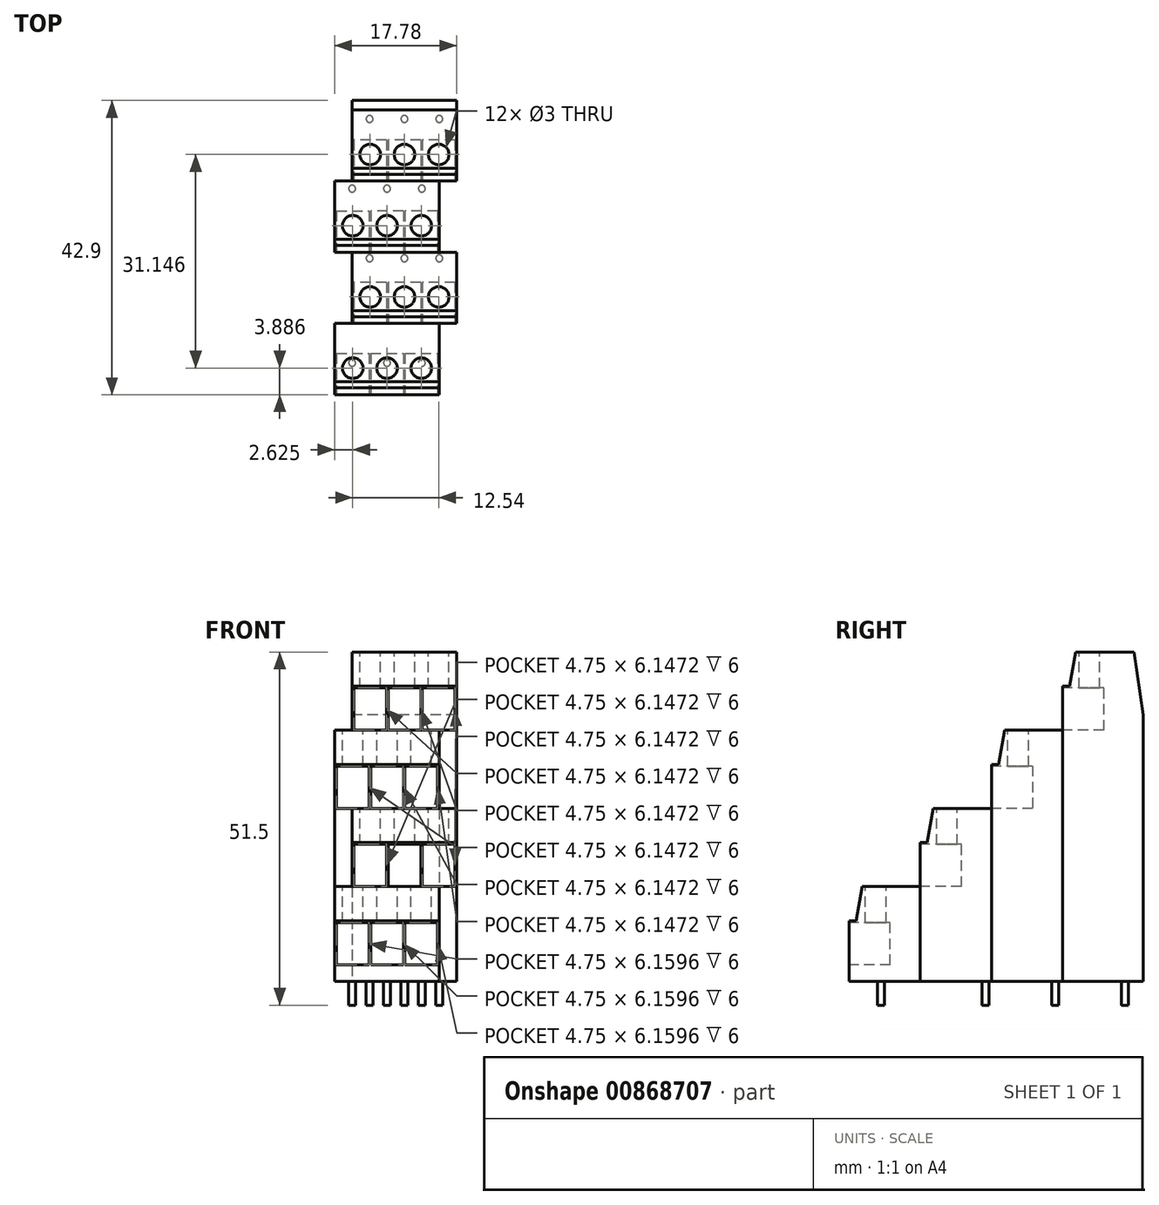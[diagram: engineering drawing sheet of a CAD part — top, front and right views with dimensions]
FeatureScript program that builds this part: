
annotation { "Feature Type Name" : "Feature", "Feature Type Description" : "" }
export const myFeature = defineFeature(function(context is Context, id is Id, definition is map)
    precondition{}
    {
        {
            var Q0;
            Q0=qCreatedBy(makeId("Right.planeOp"),FACE);
            var sketch = newSketch(context, id + "F0", { "sketchPlane" : qUnion([Q0])});
            skLineSegment(sketch, "E0.bottom", {"start": v(1.88, 24.08) * mm, "end": v(10.38, 24.08) * mm});
            skLineSegment(sketch, "E0.top", {"start": v(-31.15, -23.92) * mm, "end": v(11.75, -23.92) * mm});
            skLineSegment(sketch, "E0.left", {"start": v(-31.15, -15.12) * mm, "end": v(-31.15, -23.92) * mm});
            skLineSegment(sketch, "E0.right", {"start": v(11.75, 14.92) * mm, "end": v(11.75, -23.92) * mm});
            skPoint(sketch, "E0.middle", {"position": v(-0.86, 0) * mm});
            skLineSegment(sketch, "E1", {"start": v(-31.15, -15.12) * mm, "end": v(-30.15, -15.12) * mm});
            skLineSegment(sketch, "E2", {"start": v(-30.15, -15.12) * mm, "end": v(-29.26, -10.12) * mm});
            skLineSegment(sketch, "E3", {"start": v(-29.26, -10.12) * mm, "end": v(-20.76, -10.12) * mm});
            skLineSegment(sketch, "E4", {"start": v(-20.76, -10.12) * mm, "end": v(-20.76, -3.72) * mm});
            skLineSegment(sketch, "E5", {"start": v(-20.76, -3.72) * mm, "end": v(-19.76, -3.72) * mm});
            skLineSegment(sketch, "E6", {"start": v(-19.76, -3.72) * mm, "end": v(-18.88, 1.28) * mm});
            skLineSegment(sketch, "E7", {"start": v(-18.88, 1.28) * mm, "end": v(-10.38, 1.28) * mm});
            skLineSegment(sketch, "E8", {"start": v(-10.38, 1.28) * mm, "end": v(-10.38, 7.68) * mm});
            skLineSegment(sketch, "E9", {"start": v(-10.38, 7.68) * mm, "end": v(-9.38, 7.68) * mm});
            skLineSegment(sketch, "E10", {"start": v(-9.38, 7.68) * mm, "end": v(-8.5, 12.68) * mm});
            skLineSegment(sketch, "E11", {"start": v(-8.5, 12.68) * mm, "end": v(0, 12.68) * mm});
            skLineSegment(sketch, "E12", {"start": v(0, 12.68) * mm, "end": v(0, 19.08) * mm});
            skLineSegment(sketch, "E13", {"start": v(0, 19.08) * mm, "end": v(1, 19.08) * mm});
            skLineSegment(sketch, "E14", {"start": v(1, 19.08) * mm, "end": v(1.88, 24.08) * mm});
            skLineSegment(sketch, "E15", {"start": v(10.38, 24.08) * mm, "end": v(11.75, 14.92) * mm});
            skSolve(sketch);
        }
        {
            var Q0;
            Q0 = qSketchRegion(id + "F0", true);
            extrude(context, id + "F1", {"entities" : qUnion([Q0]), "endBound" : BoundingType.SYMMETRIC, "depth" : 17.78 * mm, "offsetDistance" : 25.4 * mm});
        }
        {
            var Q0;
            Q0=makeQuery(id+"F1.opExtrude","CAP_FACE",FACE,{"disambiguationData":[OSD([sQuery(id+"F0.wireOp",EDGE,"E0.bottom"),sQuery(id+"F0.wireOp",EDGE,"E0.top"),sQuery(id+"F0.wireOp",EDGE,"E0.left"),sQuery(id+"F0.wireOp",EDGE,"E0.right"),sQuery(id+"F0.wireOp",EDGE,"E1"),sQuery(id+"F0.wireOp",EDGE,"E2"),sQuery(id+"F0.wireOp",EDGE,"E3"),sQuery(id+"F0.wireOp",EDGE,"E4"),sQuery(id+"F0.wireOp",EDGE,"E5"),sQuery(id+"F0.wireOp",EDGE,"E6"),sQuery(id+"F0.wireOp",EDGE,"E7"),sQuery(id+"F0.wireOp",EDGE,"E8"),sQuery(id+"F0.wireOp",EDGE,"E9"),sQuery(id+"F0.wireOp",EDGE,"E10"),sQuery(id+"F0.wireOp",EDGE,"E11"),sQuery(id+"F0.wireOp",EDGE,"E12"),sQuery(id+"F0.wireOp",EDGE,"E13"),sQuery(id+"F0.wireOp",EDGE,"E14"),sQuery(id+"F0.wireOp",EDGE,"E15")])],"isStart":true});
            var sketch = newSketch(context, id + "F2", { "sketchPlane" : qUnion([Q0])});
            skLineSegment(sketch, "E16", {"start": v(20.76, -10.12) * mm, "end": v(20.76, -23.92) * mm});
            skLineSegment(sketch, "E17", {"start": v(0, 12.68) * mm, "end": v(0, -23.92) * mm});
            skLineSegment(sketch, "E18", {"start": v(10.38, 1.28) * mm, "end": v(10.38, -23.92) * mm});
            skSolve(sketch);
        }
        {
            var Q0;
            {var subQ1=sQuery(id+"F2.wireOp",EDGE,"E17");Q0=makeQuery(id+"F2.imprint","IMPRINT",FACE,{"disambiguationData":[TD([[makeQuery(id+"F2.imprint","IMPRINT",EDGE,{"derivedFrom":subQ1}),-1.0]])]});}
            var Q1;
            {var subQ1=sQuery(id+"F2.wireOp",EDGE,"E16");Q1=makeQuery(id+"F2.imprint","IMPRINT",FACE,{"disambiguationData":[TD([[makeQuery(id+"F2.imprint","IMPRINT",EDGE,{"derivedFrom":subQ1}),-1.0]])]});}
            extrude(context, id + "F3", {"entities" : qUnion([Q0, Q1]), "operationType" : NewBodyOperationType.REMOVE, "oppositeDirection" : true, "depth" : 2.54 * mm, "offsetDistance" : 25.4 * mm});
        }
        {
            var Q0;
            Q0=makeQuery(id+"F1.opExtrude","CAP_FACE",FACE,{"disambiguationData":[OSD([sQuery(id+"F0.wireOp",EDGE,"E0.bottom"),sQuery(id+"F0.wireOp",EDGE,"E0.top"),sQuery(id+"F0.wireOp",EDGE,"E0.left"),sQuery(id+"F0.wireOp",EDGE,"E0.right"),sQuery(id+"F0.wireOp",EDGE,"E1"),sQuery(id+"F0.wireOp",EDGE,"E2"),sQuery(id+"F0.wireOp",EDGE,"E3"),sQuery(id+"F0.wireOp",EDGE,"E4"),sQuery(id+"F0.wireOp",EDGE,"E5"),sQuery(id+"F0.wireOp",EDGE,"E6"),sQuery(id+"F0.wireOp",EDGE,"E7"),sQuery(id+"F0.wireOp",EDGE,"E8"),sQuery(id+"F0.wireOp",EDGE,"E9"),sQuery(id+"F0.wireOp",EDGE,"E10"),sQuery(id+"F0.wireOp",EDGE,"E11"),sQuery(id+"F0.wireOp",EDGE,"E12"),sQuery(id+"F0.wireOp",EDGE,"E13"),sQuery(id+"F0.wireOp",EDGE,"E14"),sQuery(id+"F0.wireOp",EDGE,"E15")])],"isStart":false});
            var sketch = newSketch(context, id + "F4", { "sketchPlane" : qUnion([Q0])});
            skLineSegment(sketch, "E19", {"start": v(-20.76, -10.12) * mm, "end": v(-20.76, -23.92) * mm});
            skLineSegment(sketch, "E20", {"start": v(-10.38, 1.28) * mm, "end": v(-10.38, -23.92) * mm});
            skLineSegment(sketch, "E21", {"start": v(0, 12.68) * mm, "end": v(0, -23.92) * mm});
            skSolve(sketch);
        }
        {
            var Q0;
            {var subQ1=sQuery(id+"F4.wireOp",EDGE,"E19");Q0=makeQuery(id+"F4.imprint","IMPRINT",FACE,{"disambiguationData":[TD([[makeQuery(id+"F4.imprint","IMPRINT",EDGE,{"derivedFrom":subQ1}),-1.0]])]});}
            var Q1;
            {var subQ1=sQuery(id+"F4.wireOp",EDGE,"E20");Q1=makeQuery(id+"F4.imprint","IMPRINT",FACE,{"disambiguationData":[TD([[makeQuery(id+"F4.imprint","IMPRINT",EDGE,{"derivedFrom":subQ1}),1.0]])]});}
            extrude(context, id + "F5", {"entities" : qUnion([Q0, Q1]), "operationType" : NewBodyOperationType.REMOVE, "oppositeDirection" : true, "depth" : 2.54 * mm, "offsetDistance" : 25.4 * mm});
        }
        {
            var Q0;
            Q0=makeQuery(id+"F1.opExtrude","SWEPT_FACE",FACE,{"disambiguationData":[OSD([sQuery(id+"F0.wireOp",EDGE,"E0.left")])]});
            var sketch = newSketch(context, id + "F6", { "sketchPlane" : qUnion([Q0])});
            skLineSegment(sketch, "E22.bottom", {"start": v(-8.64, -21.53) * mm, "end": v(-3.89, -21.53) * mm});
            skLineSegment(sketch, "E22.top", {"start": v(-8.64, -15.37) * mm, "end": v(-3.89, -15.37) * mm});
            skLineSegment(sketch, "E22.left", {"start": v(-8.64, -21.53) * mm, "end": v(-8.64, -15.37) * mm});
            skLineSegment(sketch, "E22.right", {"start": v(-3.89, -21.53) * mm, "end": v(-3.89, -15.37) * mm});
            skLineSegment(sketch, "E23.1.0.0", {"start": v(-3.64, -21.53) * mm, "end": v(1.11, -21.53) * mm});
            skLineSegment(sketch, "E23.1.0.1", {"start": v(-3.64, -15.37) * mm, "end": v(1.11, -15.37) * mm});
            skLineSegment(sketch, "E23.1.0.2", {"start": v(1.11, -21.53) * mm, "end": v(1.11, -15.37) * mm});
            skLineSegment(sketch, "E23.1.0.3", {"start": v(-3.64, -21.53) * mm, "end": v(-3.64, -15.37) * mm});
            skLineSegment(sketch, "E23.2.0.0", {"start": v(1.36, -21.53) * mm, "end": v(6.11, -21.53) * mm});
            skLineSegment(sketch, "E23.2.0.1", {"start": v(1.36, -15.37) * mm, "end": v(6.11, -15.37) * mm});
            skLineSegment(sketch, "E23.2.0.2", {"start": v(6.11, -21.53) * mm, "end": v(6.11, -15.37) * mm});
            skLineSegment(sketch, "E23.2.0.3", {"start": v(1.36, -21.53) * mm, "end": v(1.36, -15.37) * mm});
            skLineSegment(sketch, "E23.direction1", {"start": v(-8.64, -21.53) * mm, "end": v(-3.64, -21.53) * mm, "construction": true});
            skSolve(sketch);
        }
        {
            var Q0;
            Q0=makeQuery(id+"F5.boolean.opBoolean","MERGE",FACE,{"derivedFrom":[makeQuery(id+"F1.opExtrude","SWEPT_FACE",FACE,{"disambiguationData":[OSD([sQuery(id+"F0.wireOp",EDGE,"E4")])]})],"fromTools":[makeQuery(id+"F5.opExtrude","SWEPT_FACE",FACE,{"disambiguationData":[OSD([sQuery(id+"F4.wireOp",EDGE,"E19")])]})]});
            var sketch = newSketch(context, id + "F7", { "sketchPlane" : qUnion([Q0])});
            skLineSegment(sketch, "E24.bottom", {"start": v(-6.1, -10.12) * mm, "end": v(-1.35, -10.12) * mm});
            skLineSegment(sketch, "E24.top", {"start": v(-6.1, -3.97) * mm, "end": v(-1.35, -3.97) * mm});
            skLineSegment(sketch, "E24.left", {"start": v(-6.1, -10.12) * mm, "end": v(-6.1, -3.97) * mm});
            skLineSegment(sketch, "E24.right", {"start": v(-1.35, -10.12) * mm, "end": v(-1.35, -3.97) * mm});
            skLineSegment(sketch, "E25.1.0.0", {"start": v(-1.1, -10.12) * mm, "end": v(-1.1, -3.97) * mm});
            skLineSegment(sketch, "E25.1.0.1", {"start": v(-1.1, -3.97) * mm, "end": v(3.65, -3.97) * mm});
            skLineSegment(sketch, "E25.1.0.2", {"start": v(3.65, -10.12) * mm, "end": v(3.65, -3.97) * mm});
            skLineSegment(sketch, "E25.1.0.3", {"start": v(-1.1, -10.12) * mm, "end": v(3.65, -10.12) * mm});
            skLineSegment(sketch, "E25.2.0.0", {"start": v(3.9, -10.12) * mm, "end": v(3.9, -3.97) * mm});
            skLineSegment(sketch, "E25.2.0.1", {"start": v(3.9, -3.97) * mm, "end": v(8.65, -3.97) * mm});
            skLineSegment(sketch, "E25.2.0.2", {"start": v(8.65, -10.12) * mm, "end": v(8.65, -3.97) * mm});
            skLineSegment(sketch, "E25.2.0.3", {"start": v(3.9, -10.12) * mm, "end": v(8.65, -10.12) * mm});
            skLineSegment(sketch, "E25.direction1", {"start": v(-6.1, -10.12) * mm, "end": v(-1.1, -10.12) * mm, "construction": true});
            skSolve(sketch);
        }
        {
            var Q0;
            Q0=makeQuery(id+"F1.opExtrude","SWEPT_FACE",FACE,{"disambiguationData":[OSD([sQuery(id+"F0.wireOp",EDGE,"E8")])]});
            var sketch = newSketch(context, id + "F8", { "sketchPlane" : qUnion([Q0])});
            skLineSegment(sketch, "E26.bottom", {"start": v(-8.64, 1.28) * mm, "end": v(-3.89, 1.28) * mm});
            skLineSegment(sketch, "E26.top", {"start": v(-8.64, 7.43) * mm, "end": v(-3.9, 7.43) * mm});
            skLineSegment(sketch, "E26.left", {"start": v(-3.9, 7.43) * mm, "end": v(-3.89, 1.28) * mm});
            skLineSegment(sketch, "E26.right", {"start": v(-8.64, 7.43) * mm, "end": v(-8.64, 1.28) * mm});
            skLineSegment(sketch, "E27.1.0.0", {"start": v(-3.64, 1.28) * mm, "end": v(1.1, 1.28) * mm});
            skLineSegment(sketch, "E27.1.0.1", {"start": v(1.1, 7.43) * mm, "end": v(1.1, 1.28) * mm});
            skLineSegment(sketch, "E27.1.0.2", {"start": v(-3.64, 7.43) * mm, "end": v(-3.64, 1.28) * mm});
            skLineSegment(sketch, "E27.1.0.3", {"start": v(-3.64, 7.43) * mm, "end": v(1.1, 7.43) * mm});
            skLineSegment(sketch, "E27.2.0.0", {"start": v(1.36, 1.28) * mm, "end": v(6.1, 1.28) * mm});
            skLineSegment(sketch, "E27.2.0.1", {"start": v(6.11, 7.43) * mm, "end": v(6.11, 1.28) * mm});
            skLineSegment(sketch, "E27.2.0.2", {"start": v(1.36, 7.43) * mm, "end": v(1.36, 1.28) * mm});
            skLineSegment(sketch, "E27.2.0.3", {"start": v(1.36, 7.43) * mm, "end": v(6.1, 7.43) * mm});
            skLineSegment(sketch, "E27.direction1", {"start": v(-3.89, 1.28) * mm, "end": v(1.1, 1.28) * mm, "construction": true});
            skSolve(sketch);
        }
        {
            var Q0;
            Q0=makeQuery(id+"F5.boolean.opBoolean","MERGE",FACE,{"derivedFrom":[makeQuery(id+"F1.opExtrude","SWEPT_FACE",FACE,{"disambiguationData":[OSD([sQuery(id+"F0.wireOp",EDGE,"E12")])]})],"fromTools":[makeQuery(id+"F5.opExtrude","SWEPT_FACE",FACE,{"disambiguationData":[OSD([sQuery(id+"F4.wireOp",EDGE,"E21")])]})]});
            var sketch = newSketch(context, id + "F9", { "sketchPlane" : qUnion([Q0])});
            skLineSegment(sketch, "E28.bottom", {"start": v(-6.1, 12.68) * mm, "end": v(-1.35, 12.68) * mm});
            skLineSegment(sketch, "E28.top", {"start": v(-6.1, 18.83) * mm, "end": v(-1.35, 18.83) * mm});
            skLineSegment(sketch, "E28.left", {"start": v(-6.1, 12.68) * mm, "end": v(-6.1, 18.83) * mm});
            skLineSegment(sketch, "E28.right", {"start": v(-1.35, 12.68) * mm, "end": v(-1.35, 18.83) * mm});
            skLineSegment(sketch, "E29.1.0.0", {"start": v(-1.1, 12.68) * mm, "end": v(3.65, 12.68) * mm});
            skLineSegment(sketch, "E29.1.0.1", {"start": v(-1.1, 18.83) * mm, "end": v(3.65, 18.83) * mm});
            skLineSegment(sketch, "E29.1.0.2", {"start": v(3.65, 12.68) * mm, "end": v(3.65, 18.83) * mm});
            skLineSegment(sketch, "E29.1.0.3", {"start": v(-1.1, 12.68) * mm, "end": v(-1.1, 18.83) * mm});
            skLineSegment(sketch, "E29.2.0.0", {"start": v(3.9, 12.68) * mm, "end": v(8.65, 12.68) * mm});
            skLineSegment(sketch, "E29.2.0.1", {"start": v(3.9, 18.83) * mm, "end": v(8.65, 18.83) * mm});
            skLineSegment(sketch, "E29.2.0.2", {"start": v(8.65, 12.68) * mm, "end": v(8.65, 18.83) * mm});
            skLineSegment(sketch, "E29.2.0.3", {"start": v(3.9, 12.68) * mm, "end": v(3.9, 18.83) * mm});
            skLineSegment(sketch, "E29.direction1", {"start": v(-6.1, 12.68) * mm, "end": v(-1.1, 12.68) * mm, "construction": true});
            skSolve(sketch);
        }
        {
            var Q0;
            Q0=makeQuery(id+"F6.imprint","IMPRINT",FACE,{"disambiguationData":[TD([[makeQuery(id+"F6.imprint","IMPRINT",EDGE,{"derivedFrom":sQuery(id+"F6.wireOp",EDGE,"E22.bottom")}),1.0]])]});
            var Q1;
            Q1=makeQuery(id+"F6.imprint","IMPRINT",FACE,{"disambiguationData":[TD([[makeQuery(id+"F6.imprint","IMPRINT",EDGE,{"derivedFrom":sQuery(id+"F6.wireOp",EDGE,"E23.1.0.0")}),1.0]])]});
            var Q2;
            Q2=makeQuery(id+"F6.imprint","IMPRINT",FACE,{"disambiguationData":[TD([[makeQuery(id+"F6.imprint","IMPRINT",EDGE,{"derivedFrom":sQuery(id+"F6.wireOp",EDGE,"E23.2.0.0")}),1.0]])]});
            var Q3;
            Q3=makeQuery(id+"F8.imprint","IMPRINT",FACE,{"disambiguationData":[TD([[makeQuery(id+"F8.imprint","IMPRINT",EDGE,{"derivedFrom":sQuery(id+"F8.wireOp",EDGE,"E26.top")}),-1.0]])]});
            var Q4;
            Q4=makeQuery(id+"F8.imprint","IMPRINT",FACE,{"disambiguationData":[TD([[makeQuery(id+"F8.imprint","IMPRINT",EDGE,{"derivedFrom":sQuery(id+"F8.wireOp",EDGE,"E27.1.0.0")}),-1.0]])]});
            var Q5;
            Q5=makeQuery(id+"F8.imprint","IMPRINT",FACE,{"disambiguationData":[TD([[makeQuery(id+"F8.imprint","IMPRINT",EDGE,{"derivedFrom":sQuery(id+"F8.wireOp",EDGE,"E27.2.0.0")}),-1.0]])]});
            var Q6;
            Q6=makeQuery(id+"F7.imprint","IMPRINT",FACE,{"disambiguationData":[TD([[makeQuery(id+"F7.imprint","IMPRINT",EDGE,{"derivedFrom":sQuery(id+"F7.wireOp",EDGE,"E24.bottom")}),-1.0]])]});
            var Q7;
            Q7=makeQuery(id+"F9.imprint","IMPRINT",FACE,{"disambiguationData":[TD([[makeQuery(id+"F9.imprint","IMPRINT",EDGE,{"derivedFrom":sQuery(id+"F9.wireOp",EDGE,"E28.bottom")}),-1.0]])]});
            var Q8;
            Q8=makeQuery(id+"F9.imprint","IMPRINT",FACE,{"disambiguationData":[TD([[makeQuery(id+"F9.imprint","IMPRINT",EDGE,{"derivedFrom":sQuery(id+"F9.wireOp",EDGE,"E29.1.0.0")}),-1.0]])]});
            var Q9;
            Q9=makeQuery(id+"F9.imprint","IMPRINT",FACE,{"disambiguationData":[TD([[makeQuery(id+"F9.imprint","IMPRINT",EDGE,{"derivedFrom":sQuery(id+"F9.wireOp",EDGE,"E29.2.0.1")}),-1.0]])]});
            var Q10;
            Q10=makeQuery(id+"F7.imprint","IMPRINT",FACE,{"disambiguationData":[TD([[makeQuery(id+"F7.imprint","IMPRINT",EDGE,{"derivedFrom":sQuery(id+"F7.wireOp",EDGE,"E25.1.0.0")}),-1.0]])]});
            var Q11;
            {var subQ3=sQuery(id+"F7.wireOp",EDGE,"E25.2.0.0");Q11=makeQuery(id+"F7.imprint","IMPRINT",FACE,{"disambiguationData":[TD([[makeQuery(id+"F7.imprint","IMPRINT",EDGE,{"derivedFrom":subQ3}),-1.0]])]});}
            extrude(context, id + "F10", {"entities" : qUnion([Q0, Q1, Q2, Q3, Q4, Q5, Q6, Q7, Q8, Q9, Q10, Q11]), "operationType" : NewBodyOperationType.REMOVE, "oppositeDirection" : true, "depth" : 6 * mm, "offsetDistance" : 25.4 * mm});
        }
        {
            var Q0;
            Q0=makeQuery(id+"FIPQeaOd7nqBqoZ_1.boolean.opBoolean","MERGE",FACE,{"derivedFrom":[makeQuery(id+"F1.opExtrude","SWEPT_FACE",FACE,{"disambiguationData":[OSD([sQuery(id+"F0.wireOp",EDGE,"E3")])]})],"fromTools":[makeQuery(id+"FIPQeaOd7nqBqoZ_1.opExtrude","SWEPT_FACE",FACE,{"disambiguationData":[OSD([sQuery(id+"FcPPGYhQoeAlAkm_1.wireOp",EDGE,"nRc5gezO-lLlT-aTDT-U5ua-d5aH2JDgAWAg.bottom")])]}),makeQuery(id+"FIPQeaOd7nqBqoZ_1.opExtrude","SWEPT_FACE",FACE,{"disambiguationData":[OSD([sQuery(id+"FcPPGYhQoeAlAkm_1.wireOp",EDGE,"76d76378-90c5-41d6-9edd-ee122aa212bd.1.0.1")])]}),makeQuery(id+"FIPQeaOd7nqBqoZ_1.opExtrude","SWEPT_FACE",FACE,{"disambiguationData":[OSD([sQuery(id+"FcPPGYhQoeAlAkm_1.wireOp",EDGE,"76d76378-90c5-41d6-9edd-ee122aa212bd.2.0.1")])]})]});
            var sketch = newSketch(context, id + "F11", { "sketchPlane" : qUnion([Q0])});
            skCircle(sketch, "E30", {"center": v(-6.26, -27.26) * mm, "radius": 1.5 * mm});
            skCircle(sketch, "E31.1.0.0", {"center": v(-1.26, -27.26) * mm, "radius": 1.5 * mm});
            skCircle(sketch, "E31.2.0.0", {"center": v(3.74, -27.26) * mm, "radius": 1.5 * mm});
            skLineSegment(sketch, "E31.direction1", {"start": v(-6.26, -27.26) * mm, "end": v(-1.26, -27.26) * mm, "construction": true});
            skSolve(sketch);
        }
        {
            var Q0;
            Q0=makeQuery(id+"FhxDgFylUnVdEJf_1.boolean.opBoolean","MERGE",FACE,{"derivedFrom":[makeQuery(id+"F1.opExtrude","SWEPT_FACE",FACE,{"disambiguationData":[OSD([sQuery(id+"F0.wireOp",EDGE,"E7")])]})],"fromTools":[makeQuery(id+"FhxDgFylUnVdEJf_1.opExtrude","SWEPT_FACE",FACE,{"disambiguationData":[OSD([sQuery(id+"F8.wireOp",EDGE,"E26.bottom")])]}),makeQuery(id+"FhxDgFylUnVdEJf_1.opExtrude","SWEPT_FACE",FACE,{"disambiguationData":[OSD([sQuery(id+"F8.wireOp",EDGE,"E27.1.0.0")])]}),makeQuery(id+"FhxDgFylUnVdEJf_1.opExtrude","SWEPT_FACE",FACE,{"disambiguationData":[OSD([sQuery(id+"F8.wireOp",EDGE,"E27.2.0.0")])]})]});
            var sketch = newSketch(context, id + "F12", { "sketchPlane" : qUnion([Q0])});
            skCircle(sketch, "E32", {"center": v(-3.72, -16.88) * mm, "radius": 1.5 * mm});
            skCircle(sketch, "E33.1.0.0", {"center": v(1.28, -16.88) * mm, "radius": 1.5 * mm});
            skCircle(sketch, "E33.2.0.0", {"center": v(6.28, -16.88) * mm, "radius": 1.5 * mm});
            skLineSegment(sketch, "E33.direction1", {"start": v(-3.72, -16.88) * mm, "end": v(1.28, -16.88) * mm, "construction": true});
            skSolve(sketch);
        }
        {
            var Q0;
            Q0=makeQuery(id+"FWjFDDOlSrOGeWe_1.boolean.opBoolean","MERGE",FACE,{"derivedFrom":[makeQuery(id+"F1.opExtrude","SWEPT_FACE",FACE,{"disambiguationData":[OSD([sQuery(id+"F0.wireOp",EDGE,"E11")])]})],"fromTools":[makeQuery(id+"FWjFDDOlSrOGeWe_1.opExtrude","SWEPT_FACE",FACE,{"disambiguationData":[OSD([sQuery(id+"FboXLxqLQ1Lzw5p_1.wireOp",EDGE,"Zzgv8rQs-4HYb-RqgK-dbSt-XDPfarDPM1yx.bottom")])]}),makeQuery(id+"FWjFDDOlSrOGeWe_1.opExtrude","SWEPT_FACE",FACE,{"disambiguationData":[OSD([sQuery(id+"FboXLxqLQ1Lzw5p_1.wireOp",EDGE,"14db3bff-85f1-4a68-9081-9ea7ad831f3b.1.0.1")])]}),makeQuery(id+"FWjFDDOlSrOGeWe_1.opExtrude","SWEPT_FACE",FACE,{"disambiguationData":[OSD([sQuery(id+"FboXLxqLQ1Lzw5p_1.wireOp",EDGE,"14db3bff-85f1-4a68-9081-9ea7ad831f3b.2.0.1")])]})]});
            var sketch = newSketch(context, id + "F13", { "sketchPlane" : qUnion([Q0])});
            skCircle(sketch, "E34", {"center": v(-6.26, -6.5) * mm, "radius": 1.5 * mm});
            skCircle(sketch, "E35.1.0.0", {"center": v(-1.26, -6.5) * mm, "radius": 1.5 * mm});
            skCircle(sketch, "E35.2.0.0", {"center": v(3.74, -6.5) * mm, "radius": 1.5 * mm});
            skLineSegment(sketch, "E35.direction1", {"start": v(-6.26, -6.5) * mm, "end": v(-1.26, -6.5) * mm, "construction": true});
            skSolve(sketch);
        }
        {
            var Q0;
            Q0=makeQuery(id+"F1.opExtrude","SWEPT_FACE",FACE,{"disambiguationData":[OSD([sQuery(id+"F0.wireOp",EDGE,"E0.bottom")])]});
            var sketch = newSketch(context, id + "F14", { "sketchPlane" : qUnion([Q0])});
            skCircle(sketch, "E36", {"center": v(-3.72, 3.88) * mm, "radius": 1.5 * mm});
            skCircle(sketch, "E37.1.0.0", {"center": v(1.28, 3.88) * mm, "radius": 1.5 * mm});
            skCircle(sketch, "E37.2.0.0", {"center": v(6.28, 3.88) * mm, "radius": 1.5 * mm});
            skLineSegment(sketch, "E37.direction1", {"start": v(-3.72, 3.88) * mm, "end": v(1.28, 3.88) * mm, "construction": true});
            skSolve(sketch);
        }
        {
            var Q0;
            Q0=makeQuery(id+"F11.imprint","IMPRINT",FACE,{"disambiguationData":[TD([[makeQuery(id+"F11.imprint","IMPRINT",EDGE,{"derivedFrom":sQuery(id+"F11.wireOp",EDGE,"E30")}),1.0]])]});
            var Q1;
            Q1=makeQuery(id+"F11.imprint","IMPRINT",FACE,{"disambiguationData":[TD([[makeQuery(id+"F11.imprint","IMPRINT",EDGE,{"derivedFrom":sQuery(id+"F11.wireOp",EDGE,"E31.1.0.0")}),1.0]])]});
            var Q2;
            Q2=makeQuery(id+"F11.imprint","IMPRINT",FACE,{"disambiguationData":[TD([[makeQuery(id+"F11.imprint","IMPRINT",EDGE,{"derivedFrom":sQuery(id+"F11.wireOp",EDGE,"E31.2.0.0")}),1.0]])]});
            var Q3;
            Q3=makeQuery(id+"F12.imprint","IMPRINT",FACE,{"disambiguationData":[TD([[makeQuery(id+"F12.imprint","IMPRINT",EDGE,{"derivedFrom":sQuery(id+"F12.wireOp",EDGE,"E32")}),1.0]])]});
            var Q4;
            Q4=makeQuery(id+"F12.imprint","IMPRINT",FACE,{"disambiguationData":[TD([[makeQuery(id+"F12.imprint","IMPRINT",EDGE,{"derivedFrom":sQuery(id+"F12.wireOp",EDGE,"E33.1.0.0")}),1.0]])]});
            var Q5;
            Q5=makeQuery(id+"F12.imprint","IMPRINT",FACE,{"disambiguationData":[TD([[makeQuery(id+"F12.imprint","IMPRINT",EDGE,{"derivedFrom":sQuery(id+"F12.wireOp",EDGE,"E33.2.0.0")}),1.0]])]});
            var Q6;
            Q6=makeQuery(id+"F13.imprint","IMPRINT",FACE,{"disambiguationData":[TD([[makeQuery(id+"F13.imprint","IMPRINT",EDGE,{"derivedFrom":sQuery(id+"F13.wireOp",EDGE,"E34")}),1.0]])]});
            var Q7;
            Q7=makeQuery(id+"F13.imprint","IMPRINT",FACE,{"disambiguationData":[TD([[makeQuery(id+"F13.imprint","IMPRINT",EDGE,{"derivedFrom":sQuery(id+"F13.wireOp",EDGE,"E35.1.0.0")}),1.0]])]});
            var Q8;
            Q8=makeQuery(id+"F13.imprint","IMPRINT",FACE,{"disambiguationData":[TD([[makeQuery(id+"F13.imprint","IMPRINT",EDGE,{"derivedFrom":sQuery(id+"F13.wireOp",EDGE,"E35.2.0.0")}),1.0]])]});
            var Q9;
            Q9=makeQuery(id+"F14.imprint","IMPRINT",FACE,{"disambiguationData":[TD([[makeQuery(id+"F14.imprint","IMPRINT",EDGE,{"derivedFrom":sQuery(id+"F14.wireOp",EDGE,"E36")}),1.0]])]});
            var Q10;
            Q10=makeQuery(id+"F14.imprint","IMPRINT",FACE,{"disambiguationData":[TD([[makeQuery(id+"F14.imprint","IMPRINT",EDGE,{"derivedFrom":sQuery(id+"F14.wireOp",EDGE,"E37.1.0.0")}),1.0]])]});
            var Q11;
            Q11=makeQuery(id+"F14.imprint","IMPRINT",FACE,{"disambiguationData":[TD([[makeQuery(id+"F14.imprint","IMPRINT",EDGE,{"derivedFrom":sQuery(id+"F14.wireOp",EDGE,"E37.2.0.0")}),1.0]])]});
            extrude(context, id + "F15", {"entities" : qUnion([Q0, Q1, Q2, Q3, Q4, Q5, Q6, Q7, Q8, Q9, Q10, Q11]), "operationType" : NewBodyOperationType.REMOVE, "oppositeDirection" : true, "depth" : 6 * mm, "offsetDistance" : 25.4 * mm});
        }
        {
            var Q0;
            Q0=makeQuery(id+"F1.opExtrude","SWEPT_FACE",FACE,{"disambiguationData":[OSD([sQuery(id+"F0.wireOp",EDGE,"E0.top")])]});
            var sketch = newSketch(context, id + "F16", { "sketchPlane" : qUnion([Q0])});
            skCircle(sketch, "E38", {"center": v(3.8, 26.5) * mm, "radius": 0.5 * mm});
            skCircle(sketch, "E39.1.0.0", {"center": v(-1.27, 26.5) * mm, "radius": 0.5 * mm});
            skCircle(sketch, "E39.2.0.0", {"center": v(-6.35, 26.5) * mm, "radius": 0.5 * mm});
            skLineSegment(sketch, "E39.direction1", {"start": v(3.8, 26.5) * mm, "end": v(-1.27, 26.5) * mm, "construction": true});
            skCircle(sketch, "E40", {"center": v(3.8, 1.1) * mm, "radius": 0.5 * mm});
            skCircle(sketch, "E41.1.0.0", {"center": v(-1.27, 1.1) * mm, "radius": 0.5 * mm});
            skCircle(sketch, "E41.2.0.0", {"center": v(-6.35, 1.1) * mm, "radius": 0.5 * mm});
            skLineSegment(sketch, "E41.direction1", {"start": v(3.8, 1.1) * mm, "end": v(-1.27, 1.1) * mm, "construction": true});
            skCircle(sketch, "E42", {"center": v(6.35, 11.26) * mm, "radius": 0.5 * mm});
            skCircle(sketch, "E43.1.0.0", {"center": v(1.27, 11.26) * mm, "radius": 0.5 * mm});
            skCircle(sketch, "E43.2.0.0", {"center": v(-3.81, 11.26) * mm, "radius": 0.5 * mm});
            skLineSegment(sketch, "E43.direction1", {"start": v(6.35, 11.26) * mm, "end": v(1.27, 11.26) * mm, "construction": true});
            skCircle(sketch, "E44", {"center": v(6.35, -9.06) * mm, "radius": 0.5 * mm});
            skCircle(sketch, "E45.1.0.0", {"center": v(1.27, -9.06) * mm, "radius": 0.5 * mm});
            skCircle(sketch, "E45.2.0.0", {"center": v(-3.81, -9.06) * mm, "radius": 0.5 * mm});
            skLineSegment(sketch, "E45.direction1", {"start": v(6.35, -9.06) * mm, "end": v(1.27, -9.06) * mm, "construction": true});
            skSolve(sketch);
        }
        {
            var Q0;
            Q0=makeQuery(id+"F16.imprint","IMPRINT",FACE,{"disambiguationData":[TD([[makeQuery(id+"F16.imprint","IMPRINT",EDGE,{"derivedFrom":sQuery(id+"F16.wireOp",EDGE,"E38")}),1.0]])]});
            var Q1;
            Q1=makeQuery(id+"F16.imprint","IMPRINT",FACE,{"disambiguationData":[TD([[makeQuery(id+"F16.imprint","IMPRINT",EDGE,{"derivedFrom":sQuery(id+"F16.wireOp",EDGE,"E39.1.0.0")}),1.0]])]});
            var Q2;
            Q2=makeQuery(id+"F16.imprint","IMPRINT",FACE,{"disambiguationData":[TD([[makeQuery(id+"F16.imprint","IMPRINT",EDGE,{"derivedFrom":sQuery(id+"F16.wireOp",EDGE,"E39.2.0.0")}),1.0]])]});
            var Q3;
            Q3=makeQuery(id+"F16.imprint","IMPRINT",FACE,{"disambiguationData":[TD([[makeQuery(id+"F16.imprint","IMPRINT",EDGE,{"derivedFrom":sQuery(id+"F16.wireOp",EDGE,"E42")}),1.0]])]});
            var Q4;
            Q4=makeQuery(id+"F16.imprint","IMPRINT",FACE,{"disambiguationData":[TD([[makeQuery(id+"F16.imprint","IMPRINT",EDGE,{"derivedFrom":sQuery(id+"F16.wireOp",EDGE,"E43.1.0.0")}),1.0]])]});
            var Q5;
            Q5=makeQuery(id+"F16.imprint","IMPRINT",FACE,{"disambiguationData":[TD([[makeQuery(id+"F16.imprint","IMPRINT",EDGE,{"derivedFrom":sQuery(id+"F16.wireOp",EDGE,"E43.2.0.0")}),1.0]])]});
            var Q6;
            Q6=makeQuery(id+"F16.imprint","IMPRINT",FACE,{"disambiguationData":[TD([[makeQuery(id+"F16.imprint","IMPRINT",EDGE,{"derivedFrom":sQuery(id+"F16.wireOp",EDGE,"E41.2.0.0")}),1.0]])]});
            var Q7;
            Q7=makeQuery(id+"F16.imprint","IMPRINT",FACE,{"disambiguationData":[TD([[makeQuery(id+"F16.imprint","IMPRINT",EDGE,{"derivedFrom":sQuery(id+"F16.wireOp",EDGE,"E41.1.0.0")}),1.0]])]});
            var Q8;
            Q8=makeQuery(id+"F16.imprint","IMPRINT",FACE,{"disambiguationData":[TD([[makeQuery(id+"F16.imprint","IMPRINT",EDGE,{"derivedFrom":sQuery(id+"F16.wireOp",EDGE,"E40")}),1.0]])]});
            var Q9;
            Q9=makeQuery(id+"F16.imprint","IMPRINT",FACE,{"disambiguationData":[TD([[makeQuery(id+"F16.imprint","IMPRINT",EDGE,{"derivedFrom":sQuery(id+"F16.wireOp",EDGE,"E44")}),1.0]])]});
            var Q10;
            Q10=makeQuery(id+"F16.imprint","IMPRINT",FACE,{"disambiguationData":[TD([[makeQuery(id+"F16.imprint","IMPRINT",EDGE,{"derivedFrom":sQuery(id+"F16.wireOp",EDGE,"E45.1.0.0")}),1.0]])]});
            var Q11;
            Q11=makeQuery(id+"F16.imprint","IMPRINT",FACE,{"disambiguationData":[TD([[makeQuery(id+"F16.imprint","IMPRINT",EDGE,{"derivedFrom":sQuery(id+"F16.wireOp",EDGE,"E45.2.0.0")}),1.0]])]});
            extrude(context, id + "F17", {"entities" : qUnion([Q0, Q1, Q2, Q3, Q4, Q5, Q6, Q7, Q8, Q9, Q10, Q11]), "operationType" : NewBodyOperationType.ADD, "depth" : 3.5 * mm, "offsetDistance" : 25.4 * mm});
        }
    });
